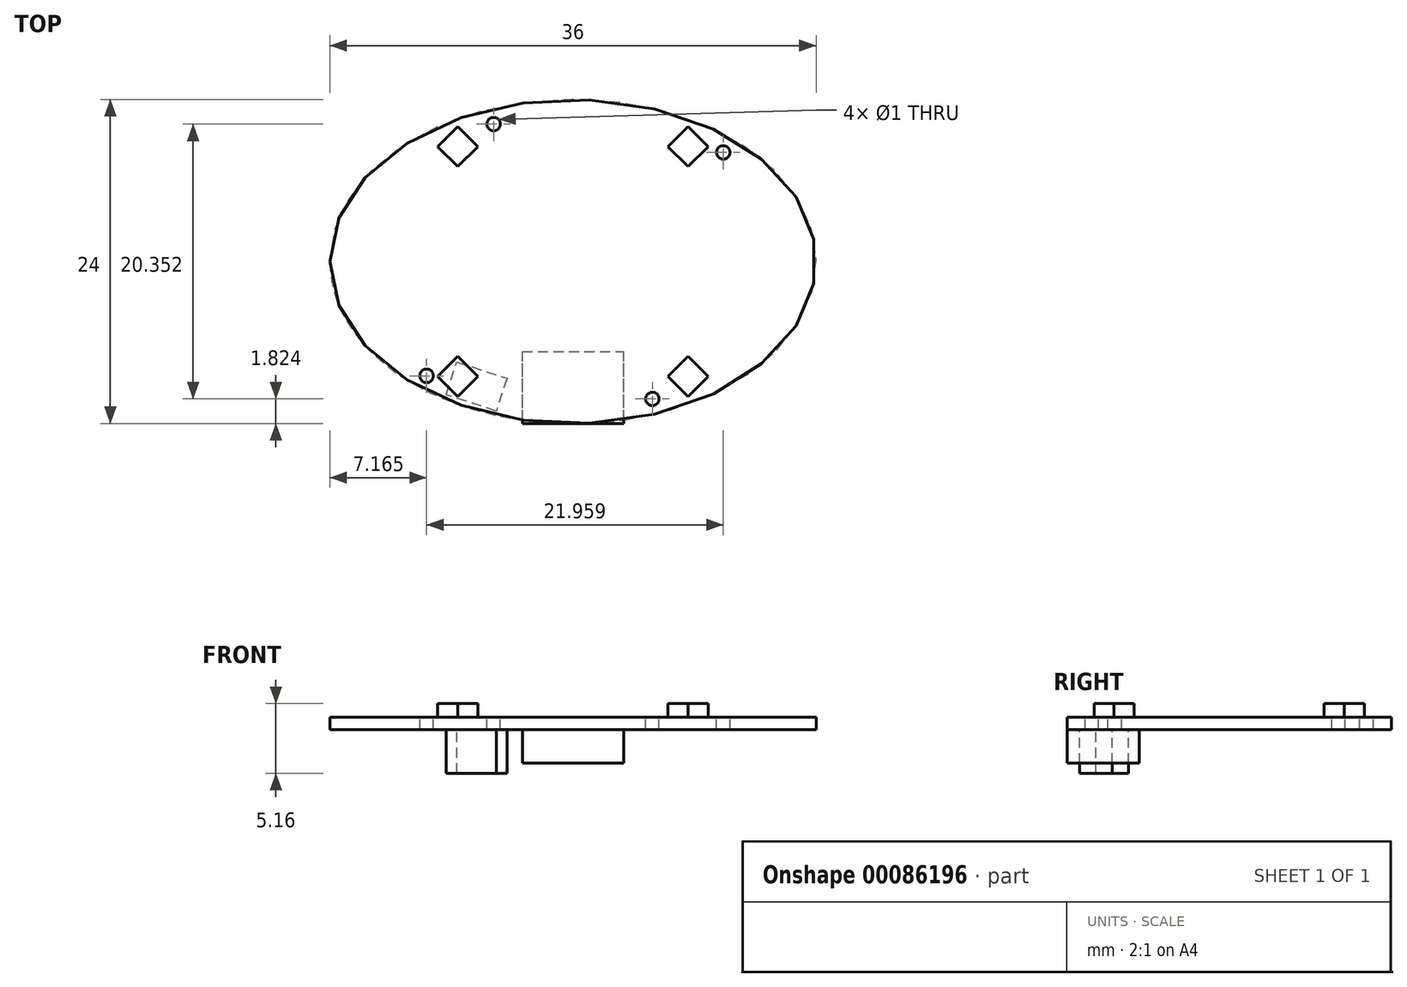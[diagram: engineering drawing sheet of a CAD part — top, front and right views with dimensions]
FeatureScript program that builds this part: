
annotation { "Feature Type Name" : "Feature", "Feature Type Description" : "" }
export const myFeature = defineFeature(function(context is Context, id is Id, definition is map)
    precondition{}
    {
        {
            var Q0;
            Q0=qCreatedBy(makeId("Top.planeOp"),FACE);
            var sketch = newSketch(context, id + "F0", { "sketchPlane" : qUnion([Q0])});
            skEllipse(sketch, "E0", {"center": v(0, 0) * mm, "majorRadius": 18 * mm, "minorRadius": 12 * mm, "majorAxis": v(-1, 0)});
            skSolve(sketch);
        }
        {
            var Q0;
            Q0 = qSketchRegion(id + "F0", true);
            extrude(context, id + "F1", {"entities" : qUnion([Q0]), "depth" : .9144 * mm});
        }
        {
            var Q0;
            Q0=makeQuery(id+"F1.opExtrude","CAP_FACE",FACE,{"disambiguationData":[OSD([sQuery(id+"F0.wireOp",EDGE,"E0")])],"isStart":false});
            var sketch = newSketch(context, id + "F2", { "sketchPlane" : qUnion([Q0])});
            skLineSegment(sketch, "E1", {"start": v(0, 0) * mm, "end": v(7.78, 7.78) * mm, "construction": true});
            skLineSegment(sketch, "E2", {"start": v(7.04, 8.52) * mm, "end": v(8.52, 7.04) * mm});
            skLineSegment(sketch, "E3", {"start": v(8.52, 7.04) * mm, "end": v(10, 8.52) * mm});
            skLineSegment(sketch, "E4", {"start": v(10, 8.52) * mm, "end": v(8.52, 10) * mm});
            skLineSegment(sketch, "E5", {"start": v(8.52, 10) * mm, "end": v(7.04, 8.52) * mm});
            skLineSegment(sketch, "E6", {"start": v(0, 0) * mm, "end": v(18, 0) * mm, "construction": true});
            skLineSegment(sketch, "E7.1.0", {"start": v(-10, 8.52) * mm, "end": v(-8.52, 7.04) * mm});
            skLineSegment(sketch, "E7.1.1", {"start": v(-8.52, 10) * mm, "end": v(-10, 8.52) * mm});
            skLineSegment(sketch, "E7.1.2", {"start": v(-7.04, 8.52) * mm, "end": v(-8.52, 10) * mm});
            skLineSegment(sketch, "E7.1.3", {"start": v(-8.52, 7.04) * mm, "end": v(-7.04, 8.52) * mm});
            skLineSegment(sketch, "E7.2.0", {"start": v(-8.52, -10) * mm, "end": v(-7.04, -8.52) * mm});
            skLineSegment(sketch, "E7.2.1", {"start": v(-10, -8.52) * mm, "end": v(-8.52, -10) * mm});
            skLineSegment(sketch, "E7.2.2", {"start": v(-8.52, -7.04) * mm, "end": v(-10, -8.52) * mm});
            skLineSegment(sketch, "E7.2.3", {"start": v(-7.04, -8.52) * mm, "end": v(-8.52, -7.04) * mm});
            skLineSegment(sketch, "E7.3.0", {"start": v(10, -8.52) * mm, "end": v(8.52, -7.04) * mm});
            skLineSegment(sketch, "E7.3.1", {"start": v(8.52, -10) * mm, "end": v(10, -8.52) * mm});
            skLineSegment(sketch, "E7.3.2", {"start": v(7.04, -8.52) * mm, "end": v(8.52, -10) * mm});
            skLineSegment(sketch, "E7.3.3", {"start": v(8.52, -7.04) * mm, "end": v(7.04, -8.52) * mm});
            skPoint(sketch, "E7.center", {"position": v(0, 0) * mm});
            skSolve(sketch);
        }
        {
            var Q0;
            Q0 = qSketchRegion(id + "F2", true);
            extrude(context, id + "F3", {"entities" : qUnion([Q0]), "operationType" : NewBodyOperationType.ADD, "depth" : 1 * mm});
        }
        {
            var Q0;
            Q0=makeQuery(id+"F1.opExtrude","CAP_FACE",FACE,{"disambiguationData":[OSD([sQuery(id+"F0.wireOp",EDGE,"E0")])],"isStart":true});
            var sketch = newSketch(context, id + "F4", { "sketchPlane" : qUnion([Q0])});
            skLineSegment(sketch, "E8.bottom", {"start": v(-3.75, 12) * mm, "end": v(3.75, 12) * mm});
            skLineSegment(sketch, "E8.top", {"start": v(-3.75, 6.67) * mm, "end": v(3.75, 6.67) * mm});
            skLineSegment(sketch, "E8.left", {"start": v(-3.75, 12) * mm, "end": v(-3.75, 6.67) * mm});
            skLineSegment(sketch, "E8.right", {"start": v(3.75, 12) * mm, "end": v(3.75, 6.67) * mm});
            skSolve(sketch);
        }
        {
            var Q0;
            Q0 = qSketchRegion(id + "F4", true);
            extrude(context, id + "F5", {"entities" : qUnion([Q0]), "operationType" : NewBodyOperationType.ADD, "depth" : 2.5 * mm});
        }
        {
            var Q0;
            Q0=makeQuery(id+"F1.opExtrude","CAP_FACE",FACE,{"disambiguationData":[OSD([sQuery(id+"F0.wireOp",EDGE,"E0")])],"isStart":true});
            var sketch = newSketch(context, id + "F6", { "sketchPlane" : qUnion([Q0])});
            skLineSegment(sketch, "E9", {"start": v(0, 0) * mm, "end": v(-6.75, 8.04) * mm, "construction": true});
            skLineSegment(sketch, "E10", {"start": v(-8.6, 7.44) * mm, "end": v(-4.9, 8.65) * mm});
            skLineSegment(sketch, "E11", {"start": v(-4.9, 8.65) * mm, "end": v(-5.68, 11.07) * mm});
            skLineSegment(sketch, "E12", {"start": v(-5.68, 11.07) * mm, "end": v(-9.4, 9.87) * mm});
            skLineSegment(sketch, "E13", {"start": v(-9.4, 9.87) * mm, "end": v(-8.6, 7.44) * mm});
            skLineSegment(sketch, "E14", {"start": v(-7.54, 10.47) * mm, "end": v(0, 0) * mm});
            skSolve(sketch);
        }
        {
            var Q0;
            Q0 = qSketchRegion(id + "F6", true);
            extrude(context, id + "F7", {"entities" : qUnion([Q0]), "operationType" : NewBodyOperationType.ADD, "depth" : 3.25 * mm});
        }
        {
            var Q0;
            Q0=makeQuery(id+"F1.opExtrude","CAP_FACE",FACE,{"disambiguationData":[OSD([sQuery(id+"F0.wireOp",EDGE,"E0")])],"isStart":false});
            var sketch = newSketch(context, id + "F8", { "sketchPlane" : qUnion([Q0])});
            skLineSegment(sketch, "E15", {"start": v(0, 0) * mm, "end": v(-5.87, 10.18) * mm, "construction": true});
            skCircle(sketch, "E16", {"center": v(-5.87, 10.18) * mm, "radius": 0.5 * mm});
            skLineSegment(sketch, "E17", {"start": v(0, 0) * mm, "end": v(18, 0) * mm, "construction": true});
            skLineSegment(sketch, "E18", {"start": v(0, 0) * mm, "end": v(11.12, 8.08) * mm, "construction": true});
            skCircle(sketch, "E19", {"center": v(11.12, 8.08) * mm, "radius": 0.5 * mm});
            skLineSegment(sketch, "E20", {"start": v(0, 0) * mm, "end": v(5.88, -10.18) * mm, "construction": true});
            skCircle(sketch, "E21", {"center": v(5.88, -10.18) * mm, "radius": 0.5 * mm});
            skLineSegment(sketch, "E22", {"start": v(0, 0) * mm, "end": v(-10.84, -8.47) * mm, "construction": true});
            skCircle(sketch, "E23", {"center": v(-10.84, -8.47) * mm, "radius": 0.5 * mm});
            skSolve(sketch);
        }
        {
            var Q0;
            Q0 = qSketchRegion(id + "F8", true);
            extrude(context, id + "F9", {"entities" : qUnion([Q0]), "operationType" : NewBodyOperationType.REMOVE, "oppositeDirection" : true, "depth" : 25 * mm});
        }
    });
